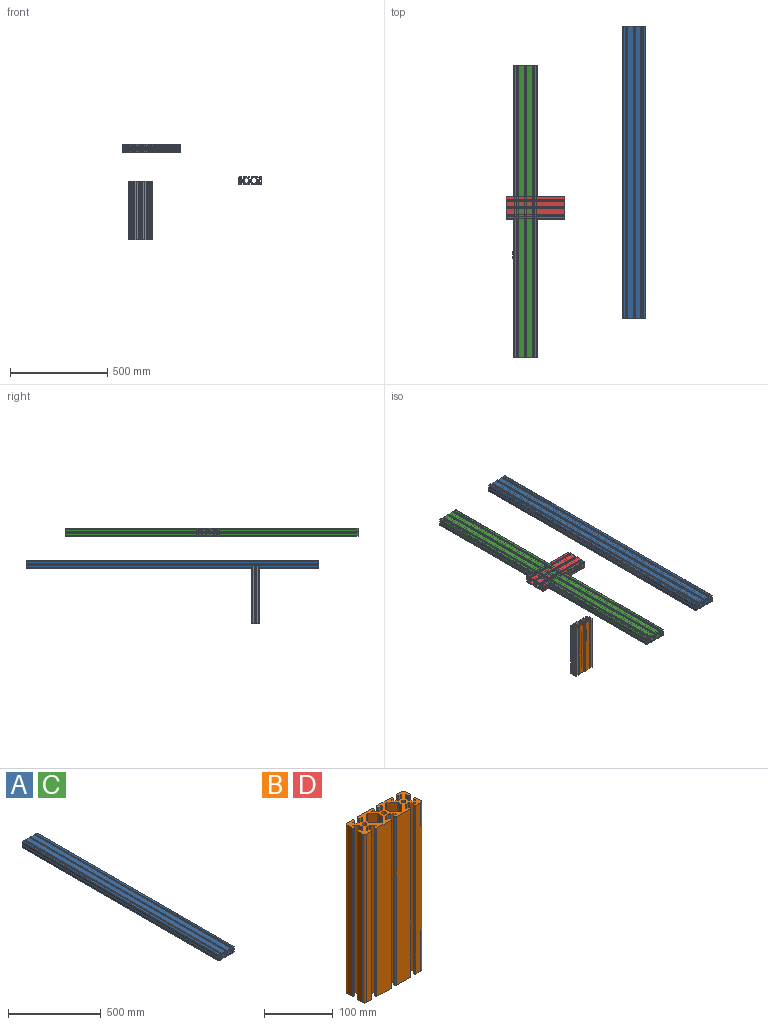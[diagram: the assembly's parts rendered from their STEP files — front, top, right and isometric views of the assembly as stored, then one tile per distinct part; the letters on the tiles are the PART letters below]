
ASSEMBLY  parts=4 mates=1
PART A: 165 faces, bbox 120x1500x40 mm
  f0: cylinder r=1.08mm len=1500mm, axis (0,-1,0), area 3586mm2, adj f21,f22,f154,f155
  f1: cylinder r=1.08mm len=1500mm, axis (0,-1,0), area 3586mm2, adj f21,f22,f146,f147
  f2: cylinder r=1.08mm len=1500mm, axis (0,-1,0), area 3586mm2, adj f21,f22,f109,f110
  f3: cylinder r=1.08mm len=1500mm, axis (0,-1,0), area 3586mm2, adj f21,f22,f95,f96
  f4: cylinder r=1.08mm len=1500mm, axis (0,-1,0), area 3586mm2, adj f21,f22,f81,f82
  f5: cylinder r=1.08mm len=1500mm, axis (0,-1,0), area 3586mm2, adj f21,f22,f47,f60
  f6: cylinder r=3.4mm len=1500mm, axis (0,-1,0), area 32044.2mm2, adj f21,f22
  f7: cylinder r=3.4mm len=1500mm, axis (0,-1,0), area 32044.2mm2, adj f21,f22
  f8: cylinder r=3.4mm len=1500mm, axis (0,-1,0), area 32044.2mm2, adj f21,f22
  f9: plane 1500x29mm, normal (0,0,-1), area 43500mm2, adj f21,f22,f51,f151
  f10: plane 1500x29mm, normal (0,0,-1), area 43500mm2, adj f21,f22,f150,f164
  f11: plane 1500x10.5mm, normal (0,0,-1), area 15750mm2, adj f21,f22,f136,f137
  f12: plane 1500x10.5mm, normal (0,0,-1), area 15750mm2, adj f21,f22,f50,f61
  f13: plane 1500x10.5mm, normal (-1,0,0), area 15750mm2, adj f21,f22,f135,f136
  f14: plane 1500x10.5mm, normal (-1,0,0), area 15750mm2, adj f21,f22,f120,f121
  f15: plane 1500x10.5mm, normal (0,0,1), area 15750mm2, adj f21,f22,f119,f120
  f16: plane 1500x29mm, normal (0,0,1), area 43500mm2, adj f21,f22,f105,f106
  f17: plane 1500x29mm, normal (0,0,1), area 43500mm2, adj f21,f22,f91,f92
  f18: plane 1500x10.5mm, normal (0,0,1), area 15750mm2, adj f21,f22,f77,f78
  f19: plane 1500x10.5mm, normal (1,0,0), area 15750mm2, adj f21,f22,f76,f77
  f20: plane 1500x10.5mm, normal (1,0,0), area 15750mm2, adj f21,f22,f61,f62
  f21: plane 120x40mm, normal (0,-1,0), area 2463.1mm2, adj f0,f1,f2,f3,f4,f5,f6,f7
  f22: plane 120x40mm, normal (0,1,0), area 2463.1mm2, adj f0,f1,f2,f3,f4,f5,f6,f7
  f23: cylinder r=1.5mm len=1500mm, axis (0,-1,0), area 1767.1mm2, adj f21,f22,f24,f34
  f24: plane 1500x6.39mm, normal (-1,0,0), area 9588.9mm2, adj f21,f22,f23,f25
  f25: cylinder r=1.5mm len=1500mm, axis (0,-1,0), area 1767.1mm2, adj f21,f22,f24,f26
  f26: plane 1500x10.75mm, normal (-0.71,0,0.71), area 22804.2mm2, adj f21,f22,f25,f27
  f27: cylinder r=1.5mm len=1500mm, axis (0,-1,0), area 3534.3mm2, adj f21,f22,f26,f28
  f28: plane 1500x10.75mm, normal (0.71,0,0.71), area 22804.2mm2, adj f21,f22,f27,f29
  f29: cylinder r=1.5mm len=1500mm, axis (0,-1,0), area 1767.1mm2, adj f21,f22,f28,f30
  f30: plane 1500x6.39mm, normal (1,0,0), area 9588.9mm2, adj f21,f22,f29,f31
  f31: cylinder r=1.5mm len=1500mm, axis (0,-1,0), area 1767.1mm2, adj f21,f22,f30,f32
  f32: plane 1500x10.75mm, normal (0.71,0,-0.71), area 22804.2mm2, adj f21,f22,f31,f33
  f33: cylinder r=1.5mm len=1500mm, axis (0,-1,0), area 3534.3mm2, adj f21,f22,f32,f34
  f34: plane 1500x10.75mm, normal (-0.71,0,-0.71), area 22804.2mm2, adj f21,f22,f23,f33
  f35: cylinder r=1.5mm len=1500mm, axis (0,-1,0), area 1767.1mm2, adj f21,f22,f36,f46
  f36: plane 1500x6.39mm, normal (-1,0,0), area 9588.9mm2, adj f21,f22,f35,f37
  f37: cylinder r=1.5mm len=1500mm, axis (0,-1,0), area 1767.1mm2, adj f21,f22,f36,f38
  f38: plane 1500x10.75mm, normal (-0.71,0,0.71), area 22804.2mm2, adj f21,f22,f37,f39
  f39: cylinder r=1.5mm len=1500mm, axis (0,-1,0), area 3534.3mm2, adj f21,f22,f38,f40
  f40: plane 1500x10.75mm, normal (0.71,0,0.71), area 22804.2mm2, adj f21,f22,f39,f41
  f41: cylinder r=1.5mm len=1500mm, axis (0,-1,0), area 1767.1mm2, adj f21,f22,f40,f42
  f42: plane 1500x6.39mm, normal (1,0,0), area 9588.9mm2, adj f21,f22,f41,f43
  f43: cylinder r=1.5mm len=1500mm, axis (0,-1,0), area 1767.1mm2, adj f21,f22,f42,f44
  f44: plane 1500x10.75mm, normal (0.71,0,-0.71), area 22804.2mm2, adj f21,f22,f43,f45
  f45: cylinder r=1.5mm len=1500mm, axis (0,-1,0), area 3534.3mm2, adj f21,f22,f44,f46
  f46: plane 1500x10.75mm, normal (-0.71,0,-0.71), area 22804.2mm2, adj f21,f22,f35,f45
  f47: plane 1500x3.92mm, normal (0,0,1), area 5874.2mm2, adj f5,f21,f22,f48
  f48: cylinder r=1mm len=1500mm, axis (0,-1,0), area 2356.2mm2, adj f21,f22,f47,f49
  f49: plane 1500x2mm, normal (-1,0,0), area 3000mm2, adj f21,f22,f48,f50
  f50: cylinder r=1.5mm len=1500mm, axis (0,-1,0), area 3534.3mm2, adj f12,f21,f22,f49
  f51: cylinder r=1.5mm len=1500mm, axis (0,-1,0), area 3534.3mm2, adj f9,f21,f22,f52
  f52: plane 1500x2mm, normal (1,0,0), area 3000mm2, adj f21,f22,f51,f53
  f53: cylinder r=1mm len=1500mm, axis (0,-1,0), area 2356.2mm2, adj f21,f22,f52,f54
  f54: plane 1500x3.92mm, normal (0,0,1), area 5874.2mm2, adj f21,f22,f53,f55
  f55: cylinder r=1.08mm len=1500mm, axis (0,-1,0), area 3586mm2, adj f21,f22,f54,f56
  f56: cylinder r=25mm len=1500mm, axis (0,-1,0), area 11115.4mm2, adj f21,f22,f55,f57
  f57: cylinder r=4mm len=1500mm, axis (0,-1,0), area 3837.1mm2, adj f21,f22,f56,f58
  f58: plane 1500x4.39mm, normal (0,0,-1), area 6579.2mm2, adj f21,f22,f57,f59
  f59: cylinder r=4mm len=1500mm, axis (0,-1,0), area 3837.1mm2, adj f21,f22,f58,f60
  f60: cylinder r=25mm len=1500mm, axis (0,-1,0), area 11115.4mm2, adj f5,f21,f22,f59
  f61: cylinder r=4mm len=1500mm, axis (0,-1,0), area 9424.8mm2, adj f12,f20,f21,f22
  f62: cylinder r=1.5mm len=1500mm, axis (0,-1,0), area 3534.3mm2, adj f20,f21,f22,f63
  f63: plane 1500x2mm, normal (0,0,1), area 3000mm2, adj f21,f22,f62,f64
  f64: cylinder r=1mm len=1500mm, axis (0,-1,0), area 2356.2mm2, adj f21,f22,f63,f65
  f65: plane 1500x3.92mm, normal (-1,0,0), area 5874.2mm2, adj f21,f22,f64,f66
  f66: cylinder r=1.08mm len=1500mm, axis (0,-1,0), area 3586mm2, adj f21,f22,f65,f67
  f67: cylinder r=25mm len=1500mm, axis (0,-1,0), area 11115.4mm2, adj f21,f22,f66,f68
  f68: cylinder r=4mm len=1500mm, axis (0,-1,0), area 3837.1mm2, adj f21,f22,f67,f69
  f69: plane 1500x4.39mm, normal (1,0,0), area 6579.2mm2, adj f21,f22,f68,f70
  f70: cylinder r=4mm len=1500mm, axis (0,-1,0), area 3837.1mm2, adj f21,f22,f69,f71
  f71: cylinder r=25mm len=1500mm, axis (0,-1,0), area 11115.4mm2, adj f21,f22,f70,f72
  f72: cylinder r=1.08mm len=1500mm, axis (0,-1,0), area 3586mm2, adj f21,f22,f71,f73
  f73: plane 1500x3.92mm, normal (-1,0,0), area 5874.2mm2, adj f21,f22,f72,f74
  f74: cylinder r=1mm len=1500mm, axis (0,-1,0), area 2356.2mm2, adj f21,f22,f73,f75
  f75: plane 1500x2mm, normal (0,0,-1), area 3000mm2, adj f21,f22,f74,f76
  f76: cylinder r=1.5mm len=1500mm, axis (0,-1,0), area 3534.3mm2, adj f19,f21,f22,f75
  f77: cylinder r=4mm len=1500mm, axis (0,-1,0), area 9424.8mm2, adj f18,f19,f21,f22
  f78: cylinder r=1.5mm len=1500mm, axis (0,-1,0), area 3534.3mm2, adj f18,f21,f22,f79
  f79: plane 1500x2mm, normal (-1,0,0), area 3000mm2, adj f21,f22,f78,f80
  f80: cylinder r=1mm len=1500mm, axis (0,-1,0), area 2356.2mm2, adj f21,f22,f79,f81
  f81: plane 1500x3.92mm, normal (0,0,-1), area 5874.2mm2, adj f4,f21,f22,f80
  f82: cylinder r=25mm len=1500mm, axis (0,-1,0), area 11115.4mm2, adj f4,f21,f22,f83
  f83: cylinder r=4mm len=1500mm, axis (0,-1,0), area 3837.1mm2, adj f21,f22,f82,f84
  f84: plane 1500x4.39mm, normal (0,0,1), area 6579.2mm2, adj f21,f22,f83,f85
  f85: cylinder r=4mm len=1500mm, axis (0,-1,0), area 3837.1mm2, adj f21,f22,f84,f86
  f86: cylinder r=25mm len=1500mm, axis (0,-1,0), area 11115.4mm2, adj f21,f22,f85,f87
  f87: cylinder r=1.08mm len=1500mm, axis (0,-1,0), area 3586mm2, adj f21,f22,f86,f88
  f88: plane 1500x3.92mm, normal (0,0,-1), area 5874.2mm2, adj f21,f22,f87,f89
  f89: cylinder r=1mm len=1500mm, axis (0,-1,0), area 2356.2mm2, adj f21,f22,f88,f90
  f90: plane 1500x2mm, normal (1,0,0), area 3000mm2, adj f21,f22,f89,f91
  f91: cylinder r=1.5mm len=1500mm, axis (0,-1,0), area 3534.3mm2, adj f17,f21,f22,f90
  f92: cylinder r=1.5mm len=1500mm, axis (0,-1,0), area 3534.3mm2, adj f17,f21,f22,f93
  f93: plane 1500x2mm, normal (-1,0,0), area 3000mm2, adj f21,f22,f92,f94
  f94: cylinder r=1mm len=1500mm, axis (0,-1,0), area 2356.2mm2, adj f21,f22,f93,f95
  f95: plane 1500x3.92mm, normal (0,0,-1), area 5874.2mm2, adj f3,f21,f22,f94
  f96: cylinder r=25mm len=1500mm, axis (0,-1,0), area 11115.4mm2, adj f3,f21,f22,f97
  f97: cylinder r=4mm len=1500mm, axis (0,-1,0), area 3837.1mm2, adj f21,f22,f96,f98
  f98: plane 1500x4.39mm, normal (0,0,1), area 6579.2mm2, adj f21,f22,f97,f99
  f99: cylinder r=4mm len=1500mm, axis (0,-1,0), area 3837.1mm2, adj f21,f22,f98,f100
  f100: cylinder r=25mm len=1500mm, axis (0,-1,0), area 11115.4mm2, adj f21,f22,f99,f101
  f101: cylinder r=1.08mm len=1500mm, axis (0,-1,0), area 3586mm2, adj f21,f22,f100,f102
  f102: plane 1500x3.92mm, normal (0,0,-1), area 5874.2mm2, adj f21,f22,f101,f103
  f103: cylinder r=1mm len=1500mm, axis (0,-1,0), area 2356.2mm2, adj f21,f22,f102,f104
  f104: plane 1500x2mm, normal (1,0,0), area 3000mm2, adj f21,f22,f103,f105
  f105: cylinder r=1.5mm len=1500mm, axis (0,-1,0), area 3534.3mm2, adj f16,f21,f22,f104
  f106: cylinder r=1.5mm len=1500mm, axis (0,-1,0), area 3534.3mm2, adj f16,f21,f22,f107
  f107: plane 1500x2mm, normal (-1,0,0), area 3000mm2, adj f21,f22,f106,f108
  f108: cylinder r=1mm len=1500mm, axis (0,-1,0), area 2356.2mm2, adj f21,f22,f107,f109
  f109: plane 1500x3.92mm, normal (0,0,-1), area 5874.2mm2, adj f2,f21,f22,f108
  f110: cylinder r=25mm len=1500mm, axis (0,-1,0), area 11115.4mm2, adj f2,f21,f22,f111
  f111: cylinder r=4mm len=1500mm, axis (0,-1,0), area 3837.1mm2, adj f21,f22,f110,f112
  f112: plane 1500x4.39mm, normal (0,0,1), area 6579.2mm2, adj f21,f22,f111,f113
  f113: cylinder r=4mm len=1500mm, axis (0,-1,0), area 3837.1mm2, adj f21,f22,f112,f114
  f114: cylinder r=25mm len=1500mm, axis (0,-1,0), area 11115.4mm2, adj f21,f22,f113,f115
  f115: cylinder r=1.08mm len=1500mm, axis (0,-1,0), area 3586mm2, adj f21,f22,f114,f116
  f116: plane 1500x3.92mm, normal (0,0,-1), area 5874.2mm2, adj f21,f22,f115,f117
  f117: cylinder r=1mm len=1500mm, axis (0,-1,0), area 2356.2mm2, adj f21,f22,f116,f118
  f118: plane 1500x2mm, normal (1,0,0), area 3000mm2, adj f21,f22,f117,f119
  f119: cylinder r=1.5mm len=1500mm, axis (0,-1,0), area 3534.3mm2, adj f15,f21,f22,f118
  f120: cylinder r=4mm len=1500mm, axis (0,-1,0), area 9424.8mm2, adj f14,f15,f21,f22
  f121: cylinder r=1.5mm len=1500mm, axis (0,-1,0), area 3534.3mm2, adj f14,f21,f22,f122
  f122: plane 1500x2mm, normal (0,0,-1), area 3000mm2, adj f21,f22,f121,f123
  f123: cylinder r=1mm len=1500mm, axis (0,-1,0), area 2356.2mm2, adj f21,f22,f122,f124
  f124: plane 1500x3.92mm, normal (1,0,0), area 5874.2mm2, adj f21,f22,f123,f125
  f125: cylinder r=1.08mm len=1500mm, axis (0,-1,0), area 3586mm2, adj f21,f22,f124,f126
  f126: cylinder r=25mm len=1500mm, axis (0,-1,0), area 11115.4mm2, adj f21,f22,f125,f127
  f127: cylinder r=4mm len=1500mm, axis (0,-1,0), area 3837.1mm2, adj f21,f22,f126,f128
  f128: plane 1500x4.39mm, normal (-1,0,0), area 6579.2mm2, adj f21,f22,f127,f129
  f129: cylinder r=4mm len=1500mm, axis (0,-1,0), area 3837.1mm2, adj f21,f22,f128,f130
  f130: cylinder r=25mm len=1500mm, axis (0,-1,0), area 11115.4mm2, adj f21,f22,f129,f131
  f131: cylinder r=1.08mm len=1500mm, axis (0,-1,0), area 3586mm2, adj f21,f22,f130,f132
  f132: plane 1500x3.92mm, normal (1,0,0), area 5874.2mm2, adj f21,f22,f131,f133
  f133: cylinder r=1mm len=1500mm, axis (0,-1,0), area 2356.2mm2, adj f21,f22,f132,f134
  f134: plane 1500x2mm, normal (0,0,1), area 3000mm2, adj f21,f22,f133,f135
  f135: cylinder r=1.5mm len=1500mm, axis (0,-1,0), area 3534.3mm2, adj f13,f21,f22,f134
  f136: cylinder r=4mm len=1500mm, axis (0,-1,0), area 9424.8mm2, adj f11,f13,f21,f22
  f137: cylinder r=1.5mm len=1500mm, axis (0,-1,0), area 3534.3mm2, adj f11,f21,f22,f138
  f138: plane 1500x2mm, normal (1,0,0), area 3000mm2, adj f21,f22,f137,f139
  f139: cylinder r=1mm len=1500mm, axis (0,-1,0), area 2356.2mm2, adj f21,f22,f138,f140
  f140: plane 1500x3.92mm, normal (0,0,1), area 5874.2mm2, adj f21,f22,f139,f141
  f141: cylinder r=1.08mm len=1500mm, axis (0,-1,0), area 3586mm2, adj f21,f22,f140,f142
  f142: cylinder r=25mm len=1500mm, axis (0,-1,0), area 11115.4mm2, adj f21,f22,f141,f143
  f143: cylinder r=4mm len=1500mm, axis (0,-1,0), area 3837.1mm2, adj f21,f22,f142,f144
  f144: plane 1500x4.39mm, normal (0,0,-1), area 6579.2mm2, adj f21,f22,f143,f145
  f145: cylinder r=4mm len=1500mm, axis (0,-1,0), area 3837.1mm2, adj f21,f22,f144,f146
  f146: cylinder r=25mm len=1500mm, axis (0,-1,0), area 11115.4mm2, adj f1,f21,f22,f145
  f147: plane 1500x3.92mm, normal (0,0,1), area 5874.2mm2, adj f1,f21,f22,f148
  f148: cylinder r=1mm len=1500mm, axis (0,-1,0), area 2356.2mm2, adj f21,f22,f147,f149
  f149: plane 1500x2mm, normal (-1,0,0), area 3000mm2, adj f21,f22,f148,f150
  f150: cylinder r=1.5mm len=1500mm, axis (0,-1,0), area 3534.3mm2, adj f10,f21,f22,f149
  f151: cylinder r=1.5mm len=1500mm, axis (0,-1,0), area 3534.3mm2, adj f9,f21,f22,f152
  f152: plane 1500x2mm, normal (-1,0,0), area 3000mm2, adj f21,f22,f151,f153
  f153: cylinder r=1mm len=1500mm, axis (0,-1,0), area 2356.2mm2, adj f21,f22,f152,f154
  f154: plane 1500x3.92mm, normal (0,0,1), area 5874.2mm2, adj f0,f21,f22,f153
  f155: cylinder r=25mm len=1500mm, axis (0,-1,0), area 11115.4mm2, adj f0,f21,f22,f156
  f156: cylinder r=4mm len=1500mm, axis (0,-1,0), area 3837.1mm2, adj f21,f22,f155,f157
  f157: plane 1500x4.39mm, normal (0,0,-1), area 6579.2mm2, adj f21,f22,f156,f158
  f158: cylinder r=4mm len=1500mm, axis (0,-1,0), area 3837.1mm2, adj f21,f22,f157,f159
  f159: cylinder r=25mm len=1500mm, axis (0,-1,0), area 11115.4mm2, adj f21,f22,f158,f160
  f160: cylinder r=1.08mm len=1500mm, axis (0,-1,0), area 3586mm2, adj f21,f22,f159,f161
  f161: plane 1500x3.92mm, normal (0,0,1), area 5874.2mm2, adj f21,f22,f160,f162
  f162: cylinder r=1mm len=1500mm, axis (0,-1,0), area 2356.2mm2, adj f21,f22,f161,f163
  f163: plane 1500x2mm, normal (1,0,0), area 3000mm2, adj f21,f22,f162,f164
  f164: cylinder r=1.5mm len=1500mm, axis (0,-1,0), area 3534.3mm2, adj f10,f21,f22,f163
PART B: 165 faces, bbox 120x40x300 mm
  f0: cylinder r=1.08mm len=300mm, axis (0,0,1), area 717.2mm2, adj f21,f22,f154,f155
  f1: cylinder r=1.08mm len=300mm, axis (0,0,1), area 717.2mm2, adj f21,f22,f146,f147
  f2: cylinder r=1.08mm len=300mm, axis (0,0,1), area 717.2mm2, adj f21,f22,f109,f110
  f3: cylinder r=1.08mm len=300mm, axis (0,0,1), area 717.2mm2, adj f21,f22,f95,f96
  f4: cylinder r=1.08mm len=300mm, axis (0,0,1), area 717.2mm2, adj f21,f22,f81,f82
  f5: cylinder r=1.08mm len=300mm, axis (0,0,1), area 717.2mm2, adj f21,f22,f47,f60
  f6: cylinder r=3.4mm len=300mm, axis (0,0,1), area 6408.8mm2, adj f21,f22
  f7: cylinder r=3.4mm len=300mm, axis (0,0,1), area 6408.8mm2, adj f21,f22
  f8: cylinder r=3.4mm len=300mm, axis (0,0,1), area 6408.8mm2, adj f21,f22
  f9: plane 300x29mm, normal (0,-1,0), area 8700mm2, adj f21,f22,f51,f151
  f10: plane 300x29mm, normal (0,-1,0), area 8700mm2, adj f21,f22,f150,f164
  f11: plane 300x10.5mm, normal (0,-1,0), area 3150mm2, adj f21,f22,f136,f137
  f12: plane 300x10.5mm, normal (0,-1,0), area 3150mm2, adj f21,f22,f50,f61
  f13: plane 300x10.5mm, normal (-1,0,0), area 3150mm2, adj f21,f22,f135,f136
  f14: plane 300x10.5mm, normal (-1,0,0), area 3150mm2, adj f21,f22,f120,f121
  f15: plane 300x10.5mm, normal (0,1,0), area 3150mm2, adj f21,f22,f119,f120
  f16: plane 300x29mm, normal (0,1,0), area 8700mm2, adj f21,f22,f105,f106
  f17: plane 300x29mm, normal (0,1,0), area 8700mm2, adj f21,f22,f91,f92
  f18: plane 300x10.5mm, normal (0,1,0), area 3150mm2, adj f21,f22,f77,f78
  f19: plane 300x10.5mm, normal (1,0,0), area 3150mm2, adj f21,f22,f76,f77
  f20: plane 300x10.5mm, normal (1,0,0), area 3150mm2, adj f21,f22,f61,f62
  f21: plane 120x40mm, normal (0,0,1), area 2463.1mm2, adj f0,f1,f2,f3,f4,f5,f6,f7
  f22: plane 120x40mm, normal (0,0,-1), area 2463.1mm2, adj f0,f1,f2,f3,f4,f5,f6,f7
  f23: cylinder r=1.5mm len=300mm, axis (0,0,1), area 353.4mm2, adj f21,f22,f24,f34
  f24: plane 300x6.39mm, normal (-1,0,0), area 1917.8mm2, adj f21,f22,f23,f25
  f25: cylinder r=1.5mm len=300mm, axis (0,0,1), area 353.4mm2, adj f21,f22,f24,f26
  f26: plane 300x10.75mm, normal (-0.71,0.71,0), area 4560.8mm2, adj f21,f22,f25,f27
  f27: cylinder r=1.5mm len=300mm, axis (0,0,1), area 706.9mm2, adj f21,f22,f26,f28
  f28: plane 300x10.75mm, normal (0.71,0.71,0), area 4560.8mm2, adj f21,f22,f27,f29
  f29: cylinder r=1.5mm len=300mm, axis (0,0,1), area 353.4mm2, adj f21,f22,f28,f30
  f30: plane 300x6.39mm, normal (1,0,0), area 1917.8mm2, adj f21,f22,f29,f31
  f31: cylinder r=1.5mm len=300mm, axis (0,0,1), area 353.4mm2, adj f21,f22,f30,f32
  f32: plane 300x10.75mm, normal (0.71,-0.71,0), area 4560.8mm2, adj f21,f22,f31,f33
  f33: cylinder r=1.5mm len=300mm, axis (0,0,1), area 706.9mm2, adj f21,f22,f32,f34
  f34: plane 300x10.75mm, normal (-0.71,-0.71,0), area 4560.8mm2, adj f21,f22,f23,f33
  f35: cylinder r=1.5mm len=300mm, axis (0,0,1), area 353.4mm2, adj f21,f22,f36,f46
  f36: plane 300x6.39mm, normal (-1,0,0), area 1917.8mm2, adj f21,f22,f35,f37
  f37: cylinder r=1.5mm len=300mm, axis (0,0,1), area 353.4mm2, adj f21,f22,f36,f38
  f38: plane 300x10.75mm, normal (-0.71,0.71,0), area 4560.8mm2, adj f21,f22,f37,f39
  f39: cylinder r=1.5mm len=300mm, axis (0,0,1), area 706.9mm2, adj f21,f22,f38,f40
  f40: plane 300x10.75mm, normal (0.71,0.71,0), area 4560.8mm2, adj f21,f22,f39,f41
  f41: cylinder r=1.5mm len=300mm, axis (0,0,1), area 353.4mm2, adj f21,f22,f40,f42
  f42: plane 300x6.39mm, normal (1,0,0), area 1917.8mm2, adj f21,f22,f41,f43
  f43: cylinder r=1.5mm len=300mm, axis (0,0,1), area 353.4mm2, adj f21,f22,f42,f44
  f44: plane 300x10.75mm, normal (0.71,-0.71,0), area 4560.8mm2, adj f21,f22,f43,f45
  f45: cylinder r=1.5mm len=300mm, axis (0,0,1), area 706.9mm2, adj f21,f22,f44,f46
  f46: plane 300x10.75mm, normal (-0.71,-0.71,0), area 4560.8mm2, adj f21,f22,f35,f45
  f47: plane 300x3.92mm, normal (0,1,0), area 1174.8mm2, adj f5,f21,f22,f48
  f48: cylinder r=1mm len=300mm, axis (0,0,1), area 471.2mm2, adj f21,f22,f47,f49
  f49: plane 300x2mm, normal (-1,0,0), area 600mm2, adj f21,f22,f48,f50
  f50: cylinder r=1.5mm len=300mm, axis (0,0,1), area 706.9mm2, adj f12,f21,f22,f49
  f51: cylinder r=1.5mm len=300mm, axis (0,0,1), area 706.9mm2, adj f9,f21,f22,f52
  f52: plane 300x2mm, normal (1,0,0), area 600mm2, adj f21,f22,f51,f53
  f53: cylinder r=1mm len=300mm, axis (0,0,1), area 471.2mm2, adj f21,f22,f52,f54
  f54: plane 300x3.92mm, normal (0,1,0), area 1174.8mm2, adj f21,f22,f53,f55
  f55: cylinder r=1.08mm len=300mm, axis (0,0,1), area 717.2mm2, adj f21,f22,f54,f56
  f56: cylinder r=25mm len=300mm, axis (0,0,1), area 2223.1mm2, adj f21,f22,f55,f57
  f57: cylinder r=4mm len=300mm, axis (0,0,1), area 767.4mm2, adj f21,f22,f56,f58
  f58: plane 300x4.39mm, normal (0,-1,0), area 1315.8mm2, adj f21,f22,f57,f59
  f59: cylinder r=4mm len=300mm, axis (0,0,1), area 767.4mm2, adj f21,f22,f58,f60
  f60: cylinder r=25mm len=300mm, axis (0,0,1), area 2223.1mm2, adj f5,f21,f22,f59
  f61: cylinder r=4mm len=300mm, axis (0,0,1), area 1885mm2, adj f12,f20,f21,f22
  f62: cylinder r=1.5mm len=300mm, axis (0,0,1), area 706.9mm2, adj f20,f21,f22,f63
  f63: plane 300x2mm, normal (0,1,0), area 600mm2, adj f21,f22,f62,f64
  f64: cylinder r=1mm len=300mm, axis (0,0,1), area 471.2mm2, adj f21,f22,f63,f65
  f65: plane 300x3.92mm, normal (-1,0,0), area 1174.8mm2, adj f21,f22,f64,f66
  f66: cylinder r=1.08mm len=300mm, axis (0,0,1), area 717.2mm2, adj f21,f22,f65,f67
  f67: cylinder r=25mm len=300mm, axis (0,0,1), area 2223.1mm2, adj f21,f22,f66,f68
  f68: cylinder r=4mm len=300mm, axis (0,0,1), area 767.4mm2, adj f21,f22,f67,f69
  f69: plane 300x4.39mm, normal (1,0,0), area 1315.8mm2, adj f21,f22,f68,f70
  f70: cylinder r=4mm len=300mm, axis (0,0,1), area 767.4mm2, adj f21,f22,f69,f71
  f71: cylinder r=25mm len=300mm, axis (0,0,1), area 2223.1mm2, adj f21,f22,f70,f72
  f72: cylinder r=1.08mm len=300mm, axis (0,0,1), area 717.2mm2, adj f21,f22,f71,f73
  f73: plane 300x3.92mm, normal (-1,0,0), area 1174.8mm2, adj f21,f22,f72,f74
  f74: cylinder r=1mm len=300mm, axis (0,0,1), area 471.2mm2, adj f21,f22,f73,f75
  f75: plane 300x2mm, normal (0,-1,0), area 600mm2, adj f21,f22,f74,f76
  f76: cylinder r=1.5mm len=300mm, axis (0,0,1), area 706.9mm2, adj f19,f21,f22,f75
  f77: cylinder r=4mm len=300mm, axis (0,0,1), area 1885mm2, adj f18,f19,f21,f22
  f78: cylinder r=1.5mm len=300mm, axis (0,0,1), area 706.9mm2, adj f18,f21,f22,f79
  f79: plane 300x2mm, normal (-1,0,0), area 600mm2, adj f21,f22,f78,f80
  f80: cylinder r=1mm len=300mm, axis (0,0,1), area 471.2mm2, adj f21,f22,f79,f81
  f81: plane 300x3.92mm, normal (0,-1,0), area 1174.8mm2, adj f4,f21,f22,f80
  f82: cylinder r=25mm len=300mm, axis (0,0,1), area 2223.1mm2, adj f4,f21,f22,f83
  f83: cylinder r=4mm len=300mm, axis (0,0,1), area 767.4mm2, adj f21,f22,f82,f84
  f84: plane 300x4.39mm, normal (0,1,0), area 1315.8mm2, adj f21,f22,f83,f85
  f85: cylinder r=4mm len=300mm, axis (0,0,1), area 767.4mm2, adj f21,f22,f84,f86
  f86: cylinder r=25mm len=300mm, axis (0,0,1), area 2223.1mm2, adj f21,f22,f85,f87
  f87: cylinder r=1.08mm len=300mm, axis (0,0,1), area 717.2mm2, adj f21,f22,f86,f88
  f88: plane 300x3.92mm, normal (0,-1,0), area 1174.8mm2, adj f21,f22,f87,f89
  f89: cylinder r=1mm len=300mm, axis (0,0,1), area 471.2mm2, adj f21,f22,f88,f90
  f90: plane 300x2mm, normal (1,0,0), area 600mm2, adj f21,f22,f89,f91
  f91: cylinder r=1.5mm len=300mm, axis (0,0,1), area 706.9mm2, adj f17,f21,f22,f90
  f92: cylinder r=1.5mm len=300mm, axis (0,0,1), area 706.9mm2, adj f17,f21,f22,f93
  f93: plane 300x2mm, normal (-1,0,0), area 600mm2, adj f21,f22,f92,f94
  f94: cylinder r=1mm len=300mm, axis (0,0,1), area 471.2mm2, adj f21,f22,f93,f95
  f95: plane 300x3.92mm, normal (0,-1,0), area 1174.8mm2, adj f3,f21,f22,f94
  f96: cylinder r=25mm len=300mm, axis (0,0,1), area 2223.1mm2, adj f3,f21,f22,f97
  f97: cylinder r=4mm len=300mm, axis (0,0,1), area 767.4mm2, adj f21,f22,f96,f98
  f98: plane 300x4.39mm, normal (0,1,0), area 1315.8mm2, adj f21,f22,f97,f99
  f99: cylinder r=4mm len=300mm, axis (0,0,1), area 767.4mm2, adj f21,f22,f98,f100
  f100: cylinder r=25mm len=300mm, axis (0,0,1), area 2223.1mm2, adj f21,f22,f99,f101
  f101: cylinder r=1.08mm len=300mm, axis (0,0,1), area 717.2mm2, adj f21,f22,f100,f102
  f102: plane 300x3.92mm, normal (0,-1,0), area 1174.8mm2, adj f21,f22,f101,f103
  f103: cylinder r=1mm len=300mm, axis (0,0,1), area 471.2mm2, adj f21,f22,f102,f104
  f104: plane 300x2mm, normal (1,0,0), area 600mm2, adj f21,f22,f103,f105
  f105: cylinder r=1.5mm len=300mm, axis (0,0,1), area 706.9mm2, adj f16,f21,f22,f104
  f106: cylinder r=1.5mm len=300mm, axis (0,0,1), area 706.9mm2, adj f16,f21,f22,f107
  f107: plane 300x2mm, normal (-1,0,0), area 600mm2, adj f21,f22,f106,f108
  f108: cylinder r=1mm len=300mm, axis (0,0,1), area 471.2mm2, adj f21,f22,f107,f109
  f109: plane 300x3.92mm, normal (0,-1,0), area 1174.8mm2, adj f2,f21,f22,f108
  f110: cylinder r=25mm len=300mm, axis (0,0,1), area 2223.1mm2, adj f2,f21,f22,f111
  f111: cylinder r=4mm len=300mm, axis (0,0,1), area 767.4mm2, adj f21,f22,f110,f112
  f112: plane 300x4.39mm, normal (0,1,0), area 1315.8mm2, adj f21,f22,f111,f113
  f113: cylinder r=4mm len=300mm, axis (0,0,1), area 767.4mm2, adj f21,f22,f112,f114
  f114: cylinder r=25mm len=300mm, axis (0,0,1), area 2223.1mm2, adj f21,f22,f113,f115
  f115: cylinder r=1.08mm len=300mm, axis (0,0,1), area 717.2mm2, adj f21,f22,f114,f116
  f116: plane 300x3.92mm, normal (0,-1,0), area 1174.8mm2, adj f21,f22,f115,f117
  f117: cylinder r=1mm len=300mm, axis (0,0,1), area 471.2mm2, adj f21,f22,f116,f118
  f118: plane 300x2mm, normal (1,0,0), area 600mm2, adj f21,f22,f117,f119
  f119: cylinder r=1.5mm len=300mm, axis (0,0,1), area 706.9mm2, adj f15,f21,f22,f118
  f120: cylinder r=4mm len=300mm, axis (0,0,1), area 1885mm2, adj f14,f15,f21,f22
  f121: cylinder r=1.5mm len=300mm, axis (0,0,1), area 706.9mm2, adj f14,f21,f22,f122
  f122: plane 300x2mm, normal (0,-1,0), area 600mm2, adj f21,f22,f121,f123
  f123: cylinder r=1mm len=300mm, axis (0,0,1), area 471.2mm2, adj f21,f22,f122,f124
  f124: plane 300x3.92mm, normal (1,0,0), area 1174.8mm2, adj f21,f22,f123,f125
  f125: cylinder r=1.08mm len=300mm, axis (0,0,1), area 717.2mm2, adj f21,f22,f124,f126
  f126: cylinder r=25mm len=300mm, axis (0,0,1), area 2223.1mm2, adj f21,f22,f125,f127
  f127: cylinder r=4mm len=300mm, axis (0,0,1), area 767.4mm2, adj f21,f22,f126,f128
  f128: plane 300x4.39mm, normal (-1,0,0), area 1315.8mm2, adj f21,f22,f127,f129
  f129: cylinder r=4mm len=300mm, axis (0,0,1), area 767.4mm2, adj f21,f22,f128,f130
  f130: cylinder r=25mm len=300mm, axis (0,0,1), area 2223.1mm2, adj f21,f22,f129,f131
  f131: cylinder r=1.08mm len=300mm, axis (0,0,1), area 717.2mm2, adj f21,f22,f130,f132
  f132: plane 300x3.92mm, normal (1,0,0), area 1174.8mm2, adj f21,f22,f131,f133
  f133: cylinder r=1mm len=300mm, axis (0,0,1), area 471.2mm2, adj f21,f22,f132,f134
  f134: plane 300x2mm, normal (0,1,0), area 600mm2, adj f21,f22,f133,f135
  f135: cylinder r=1.5mm len=300mm, axis (0,0,1), area 706.9mm2, adj f13,f21,f22,f134
  f136: cylinder r=4mm len=300mm, axis (0,0,1), area 1885mm2, adj f11,f13,f21,f22
  f137: cylinder r=1.5mm len=300mm, axis (0,0,1), area 706.9mm2, adj f11,f21,f22,f138
  f138: plane 300x2mm, normal (1,0,0), area 600mm2, adj f21,f22,f137,f139
  f139: cylinder r=1mm len=300mm, axis (0,0,1), area 471.2mm2, adj f21,f22,f138,f140
  f140: plane 300x3.92mm, normal (0,1,0), area 1174.8mm2, adj f21,f22,f139,f141
  f141: cylinder r=1.08mm len=300mm, axis (0,0,1), area 717.2mm2, adj f21,f22,f140,f142
  f142: cylinder r=25mm len=300mm, axis (0,0,1), area 2223.1mm2, adj f21,f22,f141,f143
  f143: cylinder r=4mm len=300mm, axis (0,0,1), area 767.4mm2, adj f21,f22,f142,f144
  f144: plane 300x4.39mm, normal (0,-1,0), area 1315.8mm2, adj f21,f22,f143,f145
  f145: cylinder r=4mm len=300mm, axis (0,0,1), area 767.4mm2, adj f21,f22,f144,f146
  f146: cylinder r=25mm len=300mm, axis (0,0,1), area 2223.1mm2, adj f1,f21,f22,f145
  f147: plane 300x3.92mm, normal (0,1,0), area 1174.8mm2, adj f1,f21,f22,f148
  f148: cylinder r=1mm len=300mm, axis (0,0,1), area 471.2mm2, adj f21,f22,f147,f149
  f149: plane 300x2mm, normal (-1,0,0), area 600mm2, adj f21,f22,f148,f150
  f150: cylinder r=1.5mm len=300mm, axis (0,0,1), area 706.9mm2, adj f10,f21,f22,f149
  f151: cylinder r=1.5mm len=300mm, axis (0,0,1), area 706.9mm2, adj f9,f21,f22,f152
  f152: plane 300x2mm, normal (-1,0,0), area 600mm2, adj f21,f22,f151,f153
  f153: cylinder r=1mm len=300mm, axis (0,0,1), area 471.2mm2, adj f21,f22,f152,f154
  f154: plane 300x3.92mm, normal (0,1,0), area 1174.8mm2, adj f0,f21,f22,f153
  f155: cylinder r=25mm len=300mm, axis (0,0,1), area 2223.1mm2, adj f0,f21,f22,f156
  f156: cylinder r=4mm len=300mm, axis (0,0,1), area 767.4mm2, adj f21,f22,f155,f157
  f157: plane 300x4.39mm, normal (0,-1,0), area 1315.8mm2, adj f21,f22,f156,f158
  f158: cylinder r=4mm len=300mm, axis (0,0,1), area 767.4mm2, adj f21,f22,f157,f159
  f159: cylinder r=25mm len=300mm, axis (0,0,1), area 2223.1mm2, adj f21,f22,f158,f160
  f160: cylinder r=1.08mm len=300mm, axis (0,0,1), area 717.2mm2, adj f21,f22,f159,f161
  f161: plane 300x3.92mm, normal (0,1,0), area 1174.8mm2, adj f21,f22,f160,f162
  f162: cylinder r=1mm len=300mm, axis (0,0,1), area 471.2mm2, adj f21,f22,f161,f163
  f163: plane 300x2mm, normal (1,0,0), area 600mm2, adj f21,f22,f162,f164
  f164: cylinder r=1.5mm len=300mm, axis (0,0,1), area 706.9mm2, adj f10,f21,f22,f163
PART C: same geometry as A
PART D: same geometry as B
PLACE A t=(148.65,75.8,-15.03)mm
PLACE B t=(-414.57,-350.32,-166.46)mm
PLACE C t=(-409.84,-127.61,151.83)mm
PLACE D rot(axis=(-0.58,0.58,-0.58),120deg) t=(-359.09,-107.61,151.83)mm
MATE pin_slot D.f9 <-> C.f18  axis (0,0,1) through (-359.09,-127.61,171.83)mm
